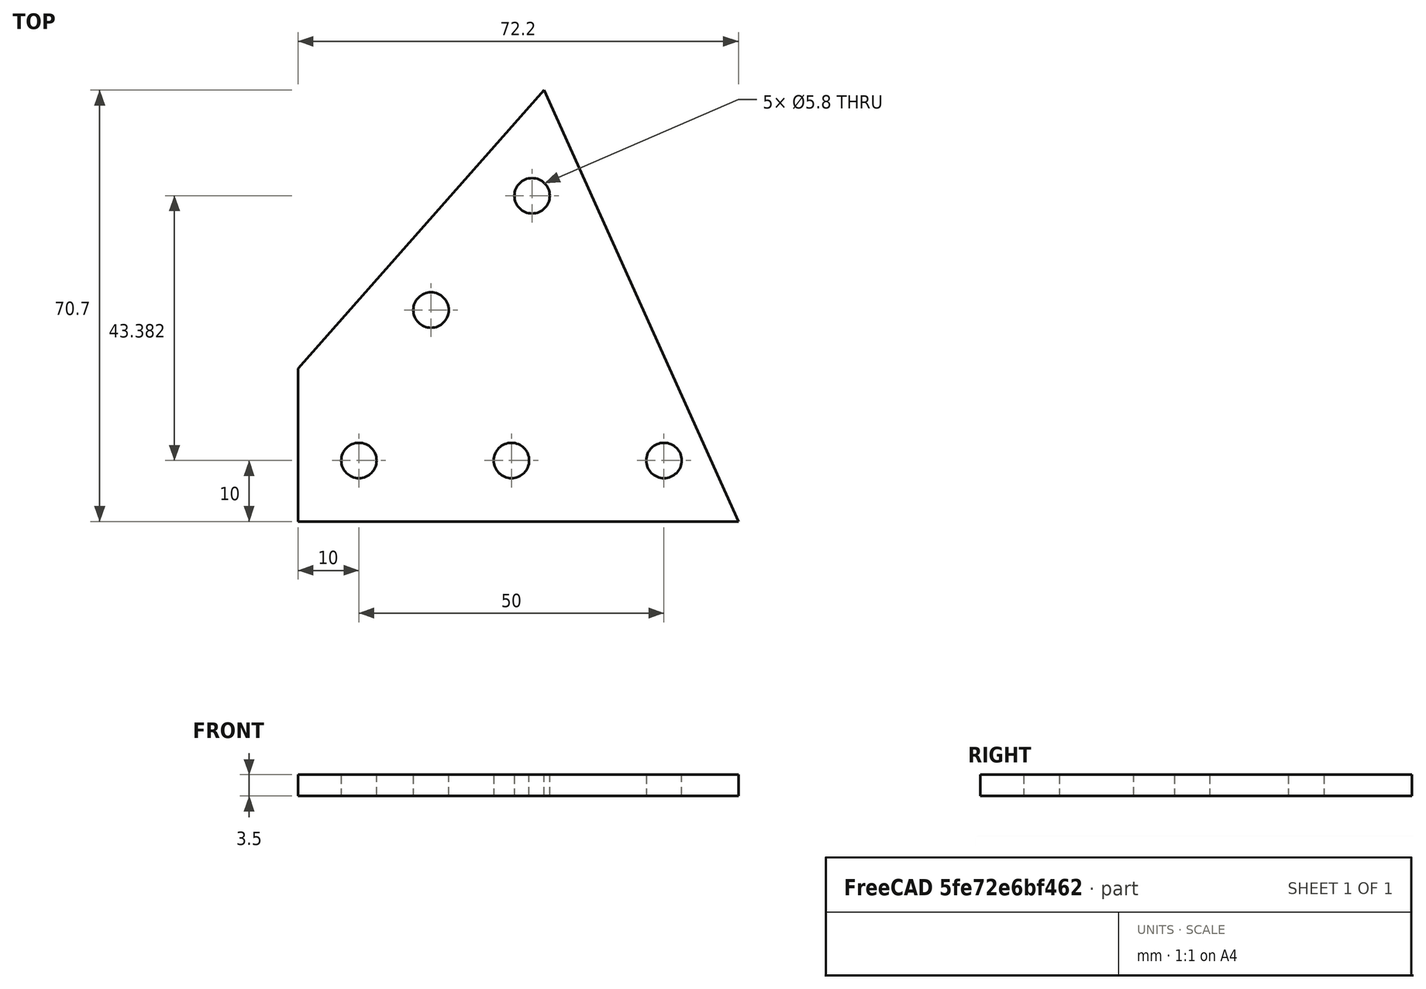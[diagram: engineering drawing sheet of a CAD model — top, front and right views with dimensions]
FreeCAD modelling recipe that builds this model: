
FCSTD DOCUMENT  (FreeCAD 0.16R6607 (Git))
Label: frame_corner_48.5_degree
License: CreativeCommons Attribution-ShareAlike
LicenseURL: http://creativecommons.org/licenses/by-sa/4.0/
objects: Sketcher::SketchObject×1, PartDesign::Pad×1
note: 3 computed .brp shape members not serialized (recipe doc carries the construction recipe); baked Part::Feature solids carry a one-line shape summary decoded from their .brp

FEATURE [Sketcher::SketchObject] Sketch
  sketch-geometry (21):
    g0: LineSegment [constr] StartX=47.8406 StartY=54.074 StartZ=0 EndX=0 EndY=0 EndZ=0
    g1: LineSegment [constr] StartX=0 StartY=0 StartZ=0 EndX=72.1992 EndY=0 EndZ=0
    g2: LineSegment [constr] StartX=0 StartY=10 StartZ=0 EndX=72.1992 EndY=10 EndZ=0
    g3: LineSegment [constr] StartX=72.1992 StartY=10 StartZ=0 EndX=72.1992 EndY=-10 EndZ=0
    g4: LineSegment [constr] StartX=72.1992 StartY=-10 StartZ=0 EndX=0 EndY=-10 EndZ=0
    g5: LineSegment [constr] StartX=0 StartY=-10 StartZ=0 EndX=0 EndY=10 EndZ=0
    g6: LineSegment [constr] StartX=7.22006 StartY=23.2524 StartZ=0 EndX=40.3511 EndY=60.7002 EndZ=0
    g7: LineSegment [constr] StartX=40.3511 StartY=60.7002 StartZ=0 EndX=55.3302 EndY=47.4478 EndZ=0
    g8: LineSegment [constr] StartX=55.3302 StartY=47.4478 StartZ=0 EndX=22.1992 EndY=10 EndZ=0
    g9: LineSegment [constr] StartX=22.1992 StartY=10 StartZ=0 EndX=7.22006 EndY=23.2524 EndZ=0
    g10: LineSegment [constr] StartX=7.22006 StartY=23.2524 StartZ=0 EndX=-22.1992 EndY=-10 EndZ=0
    g11: LineSegment [constr] StartX=-22.1992 StartY=-10 StartZ=0 EndX=0 EndY=-10 EndZ=0
    g12: LineSegment StartX=0 StartY=-10 StartZ=0 EndX=0 EndY=15.0916 EndZ=0
    g13: LineSegment StartX=0 StartY=15.0916 StartZ=0 EndX=40.3511 EndY=60.7002 EndZ=0
    g14: LineSegment StartX=40.3511 StartY=60.7002 StartZ=0 EndX=72.1992 EndY=-10 EndZ=0
    g15: LineSegment StartX=72.1992 StartY=-10 StartZ=0 EndX=0 EndY=-10 EndZ=0
    g16: Circle CenterX=21.8159 CenterY=24.6584 CenterZ=0 NormalX=0 NormalY=0 NormalZ=1 Radius=2.9
    g17: Circle CenterX=38.3814 CenterY=43.3823 CenterZ=0 NormalX=0 NormalY=0 NormalZ=1 Radius=2.9
    g18: Circle CenterX=60 CenterY=0 CenterZ=0 NormalX=0 NormalY=0 NormalZ=1 Radius=2.9
    g19: Circle CenterX=35 CenterY=0 CenterZ=0 NormalX=0 NormalY=0 NormalZ=1 Radius=2.9
    g20: Circle CenterX=10 CenterY=0 CenterZ=0 NormalX=0 NormalY=0 NormalZ=1 Radius=2.9
  constraints (58):
    c: Coincident(g0,g1)
    c: Angle(g1,g0) = 0.846485
    c: Horizontal(g1)
    c: Equal(g0,g1)
    c: Coincident(g0,g-1)
    c: Coincident(g2,g3)
    c: Coincident(g3,g4)
    c: Coincident(g4,g5)
    c: Coincident(g5,g2)
    c: Horizontal(g2)
    c: Horizontal(g4)
    c: Vertical(g3)
    c: Vertical(g5)
    c: Coincident(g6,g7)
    c: Coincident(g7,g8)
    c: Coincident(g8,g9)
    c: Coincident(g9,g6)
    c: Parallel(g6,g8)
    c: Parallel(g8,g0)
    c: Perpendicular(g8,g9)
    c: Perpendicular(g8,g7)
    c: Distance(g9) = 20
    c: DistanceY(g5) = 20
    c: PointOnObject(g0,g7)
    c: Distance(g7,g0) = 10
    c: PointOnObject(g8,g2)
    c: DistanceY(g1,g3) = -10
    c: PointOnObject(g-1,g5)
    c: PointOnObject(g1,g3)
    c: Distance(g6,g6) = 50
    c: Coincident(g10,g11)
    c: Coincident(g4,g11)
    c: Coincident(g6,g10)
    c: Angle(g11,g10) = 0.846485
    c: Horizontal(g11)
    c: Coincident(g12,g13)
    c: Coincident(g13,g14)
    c: Coincident(g14,g15)
    c: Horizontal(g15)
    c: Coincident(g4,g12)
    c: Coincident(g4,g15)
    c: PointOnObject(g12,g10)
    c: Vertical(g12)
    c: Coincident(g6,g13)
    c: Coincident(g3,g14)
    c: PointOnObject(g16,g0)
    c: PointOnObject(g20,g1)
    c: PointOnObject(g19,g1)
    c: PointOnObject(g18,g1)
    c: PointOnObject(g17,g0)
    c: Radius(g17) = 2.9
    c: Equal(g17,g16)
    c: Equal(g17,g20)
    c: Equal(g17,g19)
    c: Equal(g17,g18)
    c: Distance(g17,g16) = 25
    c: DistanceX(g19,g20) = -25
    c: DistanceX(g18,g19) = -25
FEATURE [PartDesign::Pad] Pad
  Length = 3.5
  Length2 = 100
  Sketch = -> Sketch
  Type = 0
